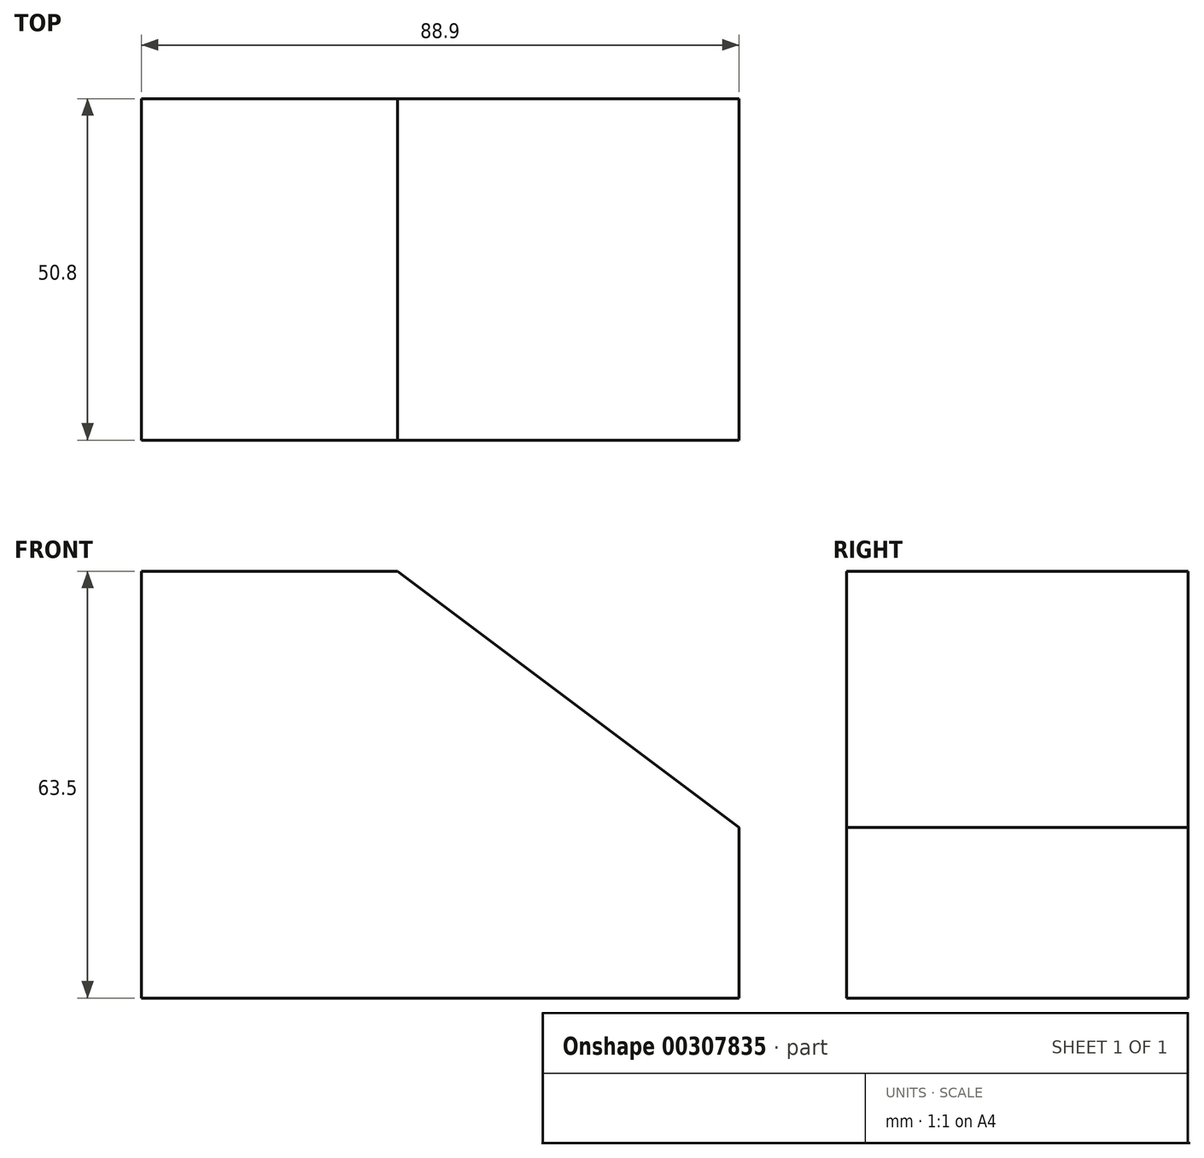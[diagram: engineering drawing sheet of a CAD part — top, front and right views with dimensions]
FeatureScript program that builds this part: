
annotation { "Feature Type Name" : "Feature", "Feature Type Description" : "" }
export const myFeature = defineFeature(function(context is Context, id is Id, definition is map)
    precondition{}
    {
        {
            var Q0;
            Q0=qCreatedBy(makeId("Front.planeOp"),FACE);
            var sketch = newSketch(context, id + "F0", { "sketchPlane" : qUnion([Q0])});
            skLineSegment(sketch, "E0", {"start": v(-38.32, -40.76) * mm, "end": v(50.58, -40.76) * mm});
            skLineSegment(sketch, "E1", {"start": v(50.58, -40.76) * mm, "end": v(50.58, -15.36) * mm});
            skLineSegment(sketch, "E2", {"start": v(-38.32, -40.76) * mm, "end": v(-38.32, 22.74) * mm});
            skLineSegment(sketch, "E3", {"start": v(-38.32, 22.74) * mm, "end": v(-0.22, 22.74) * mm});
            skLineSegment(sketch, "E4", {"start": v(-0.22, 22.74) * mm, "end": v(50.58, -15.36) * mm});
            skSolve(sketch);
        }
        {
            var Q0;
            Q0=makeQuery(id+"F0.imprint","IMPRINT",FACE,{"disambiguationData":[TD([[makeQuery(id+"F0.imprint","IMPRINT",EDGE,{"derivedFrom":sQuery(id+"F0.wireOp",EDGE,"E0")}),1.0]])]});
            extrude(context, id + "F1", {"entities" : qUnion([Q0]), "depth" : 50.8 * mm});
        }
    });
